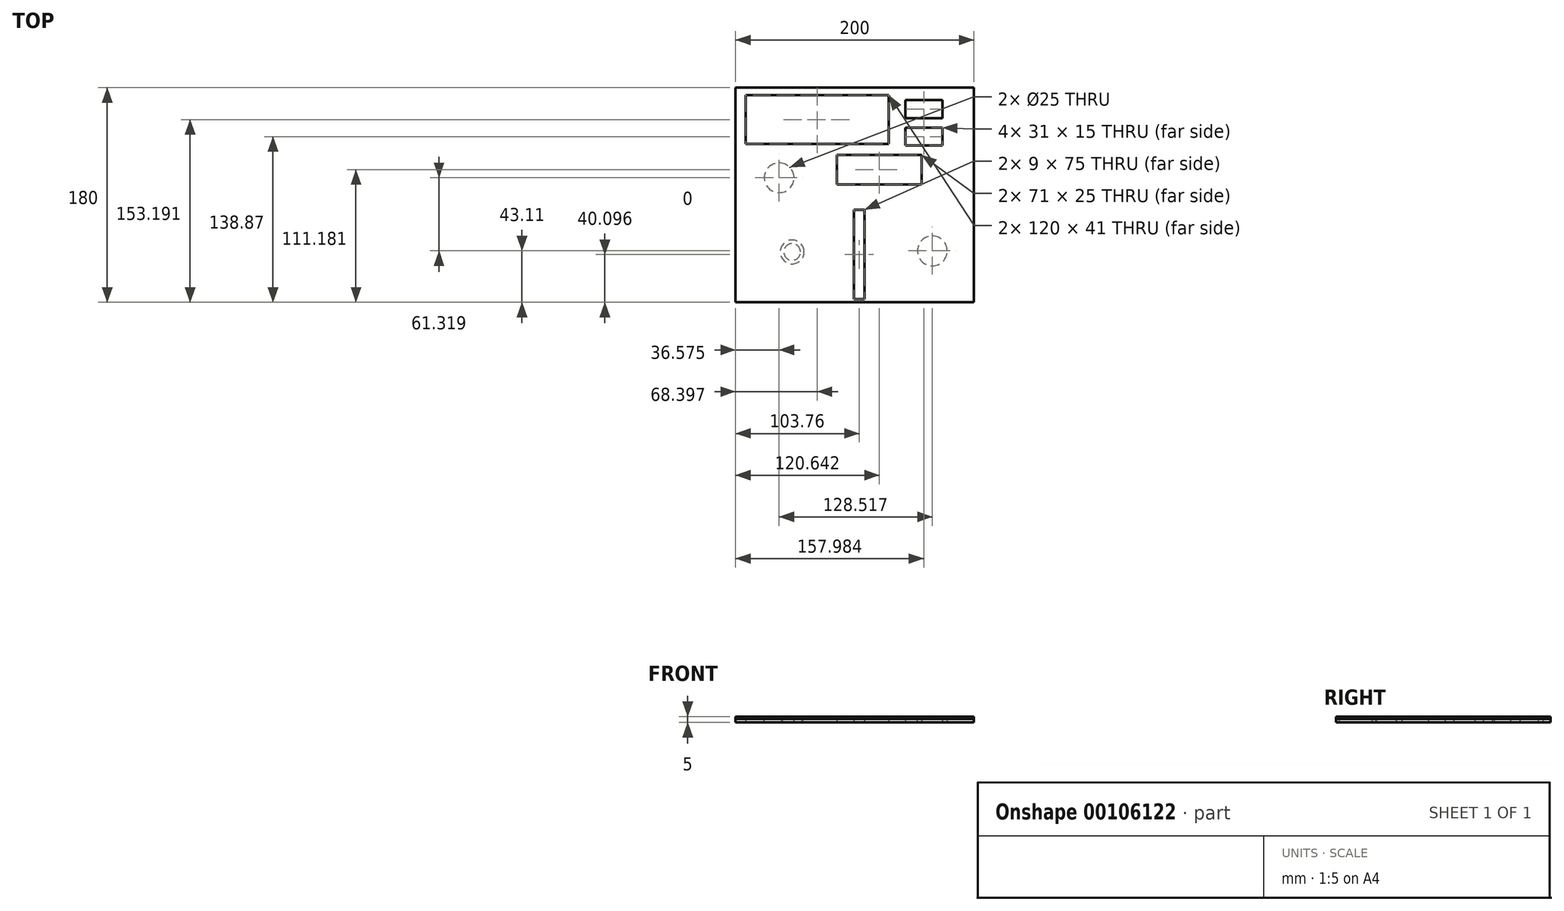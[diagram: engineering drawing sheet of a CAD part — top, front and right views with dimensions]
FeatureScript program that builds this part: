
annotation { "Feature Type Name" : "Feature", "Feature Type Description" : "" }
export const myFeature = defineFeature(function(context is Context, id is Id, definition is map)
    precondition{}
    {
        {
            var Q0;
            Q0=qCreatedBy(makeId("Top.planeOp"),FACE);
            var sketch = newSketch(context, id + "F0", { "sketchPlane" : qUnion([Q0])});
            skLineSegment(sketch, "E0.bottom", {"start": v(-99.26, 82.32) * mm, "end": v(100.74, 82.32) * mm});
            skLineSegment(sketch, "E0.top", {"start": v(-99.26, -97.68) * mm, "end": v(100.74, -97.68) * mm});
            skLineSegment(sketch, "E0.left", {"start": v(-99.26, 82.32) * mm, "end": v(-99.26, -97.68) * mm});
            skLineSegment(sketch, "E0.right", {"start": v(100.74, 82.32) * mm, "end": v(100.74, -97.68) * mm});
            skLineSegment(sketch, "E1.bottom", {"start": v(-90.86, 76.01) * mm, "end": v(29.14, 76.01) * mm});
            skLineSegment(sketch, "E1.top", {"start": v(-90.86, 35.01) * mm, "end": v(29.14, 35.01) * mm});
            skLineSegment(sketch, "E1.left", {"start": v(-90.86, 76.01) * mm, "end": v(-90.86, 35.01) * mm});
            skLineSegment(sketch, "E1.right", {"start": v(29.14, 76.01) * mm, "end": v(29.14, 35.01) * mm});
            skLineSegment(sketch, "E2.bottom", {"start": v(43.22, 71.8) * mm, "end": v(74.22, 71.8) * mm});
            skLineSegment(sketch, "E2.top", {"start": v(43.22, 56.8) * mm, "end": v(74.22, 56.8) * mm});
            skLineSegment(sketch, "E2.left", {"start": v(43.22, 71.8) * mm, "end": v(43.22, 56.8) * mm});
            skLineSegment(sketch, "E2.right", {"start": v(74.22, 71.8) * mm, "end": v(74.22, 56.8) * mm});
            skLineSegment(sketch, "E3.bottom", {"start": v(74.22, 48.69) * mm, "end": v(43.22, 48.69) * mm});
            skLineSegment(sketch, "E3.top", {"start": v(74.22, 33.69) * mm, "end": v(43.22, 33.69) * mm});
            skLineSegment(sketch, "E3.left", {"start": v(74.22, 48.69) * mm, "end": v(74.22, 33.69) * mm});
            skLineSegment(sketch, "E3.right", {"start": v(43.22, 48.69) * mm, "end": v(43.22, 33.69) * mm});
            skLineSegment(sketch, "E4.bottom", {"start": v(-14.12, 26) * mm, "end": v(56.88, 26) * mm});
            skLineSegment(sketch, "E4.top", {"start": v(-14.12, 1) * mm, "end": v(56.88, 1) * mm});
            skLineSegment(sketch, "E4.left", {"start": v(-14.12, 26) * mm, "end": v(-14.12, 1) * mm});
            skLineSegment(sketch, "E4.right", {"start": v(56.88, 26) * mm, "end": v(56.88, 1) * mm});
            skLineSegment(sketch, "E5.bottom", {"start": v(0, -20.08) * mm, "end": v(9, -20.08) * mm});
            skLineSegment(sketch, "E5.top", {"start": v(0, -95.08) * mm, "end": v(9, -95.08) * mm});
            skLineSegment(sketch, "E5.left", {"start": v(0, -20.08) * mm, "end": v(0, -95.08) * mm});
            skLineSegment(sketch, "E5.right", {"start": v(9, -20.08) * mm, "end": v(9, -95.08) * mm});
            skSolve(sketch);
        }
        {
            var Q0;
            Q0=makeQuery(id+"F0.imprint","IMPRINT",FACE,{"disambiguationData":[TD([[makeQuery(id+"F0.imprint","IMPRINT",EDGE,{"derivedFrom":sQuery(id+"F0.wireOp",EDGE,"E0.bottom")}),-1.0]])]});
            extrude(context, id + "F1", {"entities" : qUnion([Q0]), "depth" : 3 * mm});
        }
        {
            var Q0;
            Q0=makeQuery(id+"F1.opExtrude","CAP_FACE",FACE,{"disambiguationData":[OSD([sQuery(id+"F0.wireOp",EDGE,"E0.bottom"),sQuery(id+"F0.wireOp",EDGE,"E0.top"),sQuery(id+"F0.wireOp",EDGE,"E0.left"),sQuery(id+"F0.wireOp",EDGE,"E0.right")])],"isStart":false});
            var sketch = newSketch(context, id + "F2", { "sketchPlane" : qUnion([Q0])});
            skLineSegment(sketch, "E6", {"start": v(-99.26, -55.46) * mm, "end": v(-51.76, -55.46) * mm, "construction": true});
            skCircle(sketch, "E7", {"center": v(-51.76, -55.46) * mm, "radius": 5 * mm});
            skSolve(sketch);
        }
        {
            var Q0;
            Q0=makeQuery(id+"F2.imprint","IMPRINT",FACE,{"disambiguationData":[TD([[makeQuery(id+"F2.imprint","IMPRINT",EDGE,{"derivedFrom":sQuery(id+"F2.wireOp",EDGE,"E7")}),-1.0]])]});
            var sketch = newSketch(context, id + "F3", { "sketchPlane" : qUnion([Q0])});
            skLineSegment(sketch, "E8.top", {"start": v(-1, -93.43) * mm, "end": v(8, -93.43) * mm, "construction": true});
            skLineSegment(sketch, "E8.left", {"start": v(-1, -18.43) * mm, "end": v(-1, -93.43) * mm, "construction": true});
            skLineSegment(sketch, "E8.right", {"start": v(8, -18.43) * mm, "end": v(8, -93.43) * mm, "construction": true});
            skCircle(sketch, "E9", {"center": v(65.83, -54.57) * mm, "radius": 12.5 * mm});
            skCircle(sketch, "E10", {"center": v(-62.68, 6.75) * mm, "radius": 12.5 * mm});
            skSolve(sketch);
        }
        {
            var Q0;
            Q0=sQuery(id+"F2.wireOp",VERTEX,"E7.center");
            var Q1;
            Q1=makeQuery(id+"F1.opExtrude","SWEPT_BODY",BODY,{"disambiguationData":[OSD([sQuery(id+"F0.wireOp",EDGE,"E0.bottom"),sQuery(id+"F0.wireOp",EDGE,"E0.top"),sQuery(id+"F0.wireOp",EDGE,"E0.left"),sQuery(id+"F0.wireOp",EDGE,"E0.right")])]});
            hole(context, id + "F4", {"style" : HoleStyle.C_SINK, "endStyle" : HoleEndStyle.THROUGH, "holeDiameter" : 8.8 * mm, "cSinkDiameter" : 20 * mm, "cSinkAngle" : 90 * degree, "startFromSketch" : true, "locations" : qUnion([Q0]), "scope" : qUnion([Q1]), "isTappedThrough" : true});
        }
        {
            var Q0;
            Q0=sQuery(id+"F3.wireOp",VERTEX,"E9.center");
            var Q1;
            Q1=makeQuery(id+"F1.opExtrude","SWEPT_BODY",BODY,{"disambiguationData":[OSD([sQuery(id+"F0.wireOp",EDGE,"E0.bottom"),sQuery(id+"F0.wireOp",EDGE,"E0.top"),sQuery(id+"F0.wireOp",EDGE,"E0.left"),sQuery(id+"F0.wireOp",EDGE,"E0.right")])]});
            hole(context, id + "F5", {"style" : HoleStyle.SIMPLE, "endStyle" : HoleEndStyle.THROUGH, "holeDiameter" : 25 * mm, "locations" : qUnion([Q0]), "scope" : qUnion([Q1]), "isTappedThrough" : true});
        }
        {
            var Q0;
            Q0=sQuery(id+"F3.wireOp",VERTEX,"E10.center");
            var Q1;
            Q1=makeQuery(id+"F1.opExtrude","SWEPT_BODY",BODY,{"disambiguationData":[OSD([sQuery(id+"F0.wireOp",EDGE,"E0.bottom"),sQuery(id+"F0.wireOp",EDGE,"E0.top"),sQuery(id+"F0.wireOp",EDGE,"E0.left"),sQuery(id+"F0.wireOp",EDGE,"E0.right")])]});
            hole(context, id + "F6", {"style" : HoleStyle.SIMPLE, "endStyle" : HoleEndStyle.THROUGH, "holeDiameter" : 25 * mm, "locations" : qUnion([Q0]), "scope" : qUnion([Q1]), "isTappedThrough" : true});
        }
        {
            var Q0;
            Q0=makeQuery(id+"F0.imprint","IMPRINT",FACE,{"disambiguationData":[TD([[makeQuery(id+"F0.imprint","IMPRINT",EDGE,{"derivedFrom":sQuery(id+"F0.wireOp",EDGE,"E0.bottom")}),-1.0]])]});
            var sketch = newSketch(context, id + "F7", { "sketchPlane" : qUnion([Q0])});
            skCircle(sketch, "E11", {"center": v(-4.62, -33.53) * mm, "radius": 2.5 * mm});
            skCircle(sketch, "E12", {"center": v(23.05, -4.35) * mm, "radius": 2.5 * mm});
            skCircle(sketch, "E13", {"center": v(23.05, 29.54) * mm, "radius": 2.5 * mm});
            skCircle(sketch, "E14", {"center": v(59.95, 29.54) * mm, "radius": 2.5 * mm});
            skCircle(sketch, "E15", {"center": v(60.6, 76.52) * mm, "radius": 2.5 * mm});
            skCircle(sketch, "E16", {"center": v(33.35, 55.5) * mm, "radius": 2.5 * mm});
            skCircle(sketch, "E17", {"center": v(-95.15, 56.79) * mm, "radius": 2.5 * mm});
            skCircle(sketch, "E18", {"center": v(13.61, -33.31) * mm, "radius": 2.5 * mm});
            skCircle(sketch, "E19", {"center": v(13.4, -87.38) * mm, "radius": 2.5 * mm});
            skCircle(sketch, "E20", {"center": v(-5.27, -87.38) * mm, "radius": 2.5 * mm});
            skCircle(sketch, "E21", {"center": v(-7.66, -55.41) * mm, "radius": 2.5 * mm});
            skCircle(sketch, "E22", {"center": v(-92.66, -55.41) * mm, "radius": 2.5 * mm});
            skLineSegment(sketch, "E23", {"start": v(-52.03, -97.41) * mm, "end": v(-52.03, -55.41) * mm, "construction": true});
            skLineSegment(sketch, "E24", {"start": v(-99.66, -55.41) * mm, "end": v(-92.66, -55.41) * mm, "construction": true});
            skLineSegment(sketch, "E25", {"start": v(-92.66, -55.41) * mm, "end": v(-7.66, -55.41) * mm, "construction": true});
            skSolve(sketch);
        }
        {
            var Q0;
            Q0=sQuery(id+"F7.wireOp",EDGE,"E22");
            var Q1;
            Q1=sQuery(id+"F7.wireOp",EDGE,"E21");
            extrude(context, id + "F8", {"bodyType" : ToolBodyType.SURFACE, "surfaceEntities" : qUnion([Q0, Q1]), "oppositeDirection" : true, "depth" : 5 * mm});
        }
        {
            var Q0;
            Q0=sQuery(id+"F7.wireOp",EDGE,"E19");
            var Q1;
            Q1=sQuery(id+"F7.wireOp",EDGE,"E20");
            var Q2;
            Q2=sQuery(id+"F7.wireOp",EDGE,"E11");
            var Q3;
            Q3=sQuery(id+"F7.wireOp",EDGE,"E18");
            var Q4;
            Q4=sQuery(id+"F7.wireOp",EDGE,"E14");
            var Q5;
            Q5=sQuery(id+"F7.wireOp",EDGE,"E15");
            extrude(context, id + "F9", {"bodyType" : ToolBodyType.SURFACE, "surfaceEntities" : qUnion([Q0, Q1, Q2, Q3, Q4, Q5]), "oppositeDirection" : true, "depth" : 5 * mm});
        }
        {
            var Q0;
            Q0=sQuery(id+"F7.wireOp",EDGE,"E17");
            var Q1;
            Q1=sQuery(id+"F7.wireOp",EDGE,"E16");
            var Q2;
            Q2=sQuery(id+"F7.wireOp",EDGE,"E13");
            var Q3;
            Q3=sQuery(id+"F7.wireOp",EDGE,"E12");
            extrude(context, id + "F10", {"bodyType" : ToolBodyType.SURFACE, "surfaceEntities" : qUnion([Q0, Q1, Q2, Q3]), "oppositeDirection" : true, "depth" : 8 * mm});
        }
        {
            var Q0;
            Q0=makeQuery(id+"F9.opExtrude","SWEPT_BODY",BODY,{"disambiguationData":[OSD([sQuery(id+"F7.wireOp",EDGE,"E14")])]});
            var Q1;
            Q1=makeQuery(id+"F10.opExtrude","SWEPT_BODY",BODY,{"disambiguationData":[OSD([sQuery(id+"F7.wireOp",EDGE,"E13")])]});
            var Q2;
            Q2=makeQuery(id+"F10.opExtrude","SWEPT_BODY",BODY,{"disambiguationData":[OSD([sQuery(id+"F7.wireOp",EDGE,"E12")])]});
            var Q3;
            Q3=makeQuery(id+"F9.opExtrude","SWEPT_BODY",BODY,{"disambiguationData":[OSD([sQuery(id+"F7.wireOp",EDGE,"E18")])]});
            var Q4;
            Q4=makeQuery(id+"F9.opExtrude","SWEPT_BODY",BODY,{"disambiguationData":[OSD([sQuery(id+"F7.wireOp",EDGE,"E11")])]});
            var Q5;
            Q5=makeQuery(id+"F9.opExtrude","SWEPT_BODY",BODY,{"disambiguationData":[OSD([sQuery(id+"F7.wireOp",EDGE,"E15")])]});
            deleteBodies(context, id + "F11", {"entities" : qUnion([Q0, Q1, Q2, Q3, Q4, Q5])});
        }
        {
            var Q0;
            Q0=makeQuery(id+"F0.imprint","IMPRINT",FACE,{"disambiguationData":[TD([[makeQuery(id+"F0.imprint","IMPRINT",EDGE,{"derivedFrom":sQuery(id+"F0.wireOp",EDGE,"E0.bottom")}),-1.0]])]});
            extrude(context, id + "F12", {"entities" : qUnion([Q0]), "depth" : 5 * mm});
        }
    });
